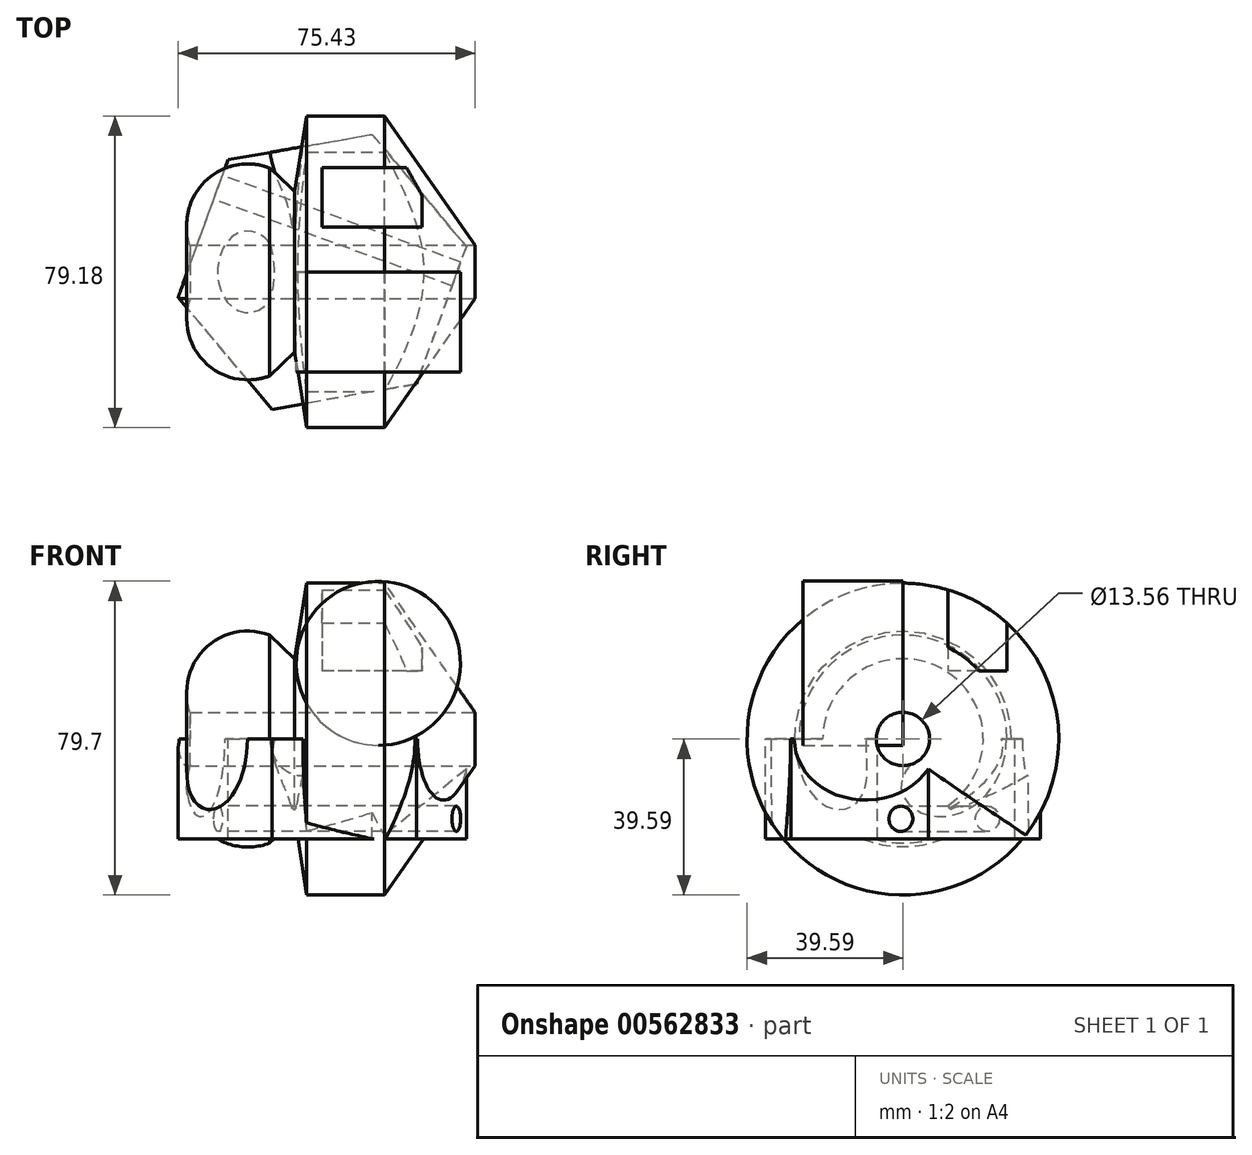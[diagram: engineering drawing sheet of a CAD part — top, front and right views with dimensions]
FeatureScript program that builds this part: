
annotation { "Feature Type Name" : "Feature", "Feature Type Description" : "" }
export const myFeature = defineFeature(function(context is Context, id is Id, definition is map)
    precondition{}
    {
        {
            var Q0;
            Q0=qCreatedBy(makeId("Top.planeOp"),FACE);
            var sketch = newSketch(context, id + "F0", { "sketchPlane" : qUnion([Q0])});
            skCircle(sketch, "E0.cCircle", {"center": v(0, 0) * mm, "radius": 32.2 * mm, "construction": true});
            skLineSegment(sketch, "E0.0", {"start": v(12.7, 34.93) * mm, "end": v(36.6, 6.47) * mm});
            skLineSegment(sketch, "E0.1", {"start": v(36.6, 6.47) * mm, "end": v(23.9, -28.47) * mm});
            skLineSegment(sketch, "E0.2", {"start": v(23.9, -28.47) * mm, "end": v(-12.7, -34.93) * mm});
            skLineSegment(sketch, "E0.3", {"start": v(-12.7, -34.93) * mm, "end": v(-36.6, -6.47) * mm});
            skLineSegment(sketch, "E0.4", {"start": v(-36.6, -6.47) * mm, "end": v(-23.9, 28.47) * mm});
            skLineSegment(sketch, "E0.5", {"start": v(-23.9, 28.47) * mm, "end": v(12.7, 34.93) * mm});
            skPoint(sketch, "E0.0.midPoint", {"position": v(24.65, 20.7) * mm});
            skSolve(sketch);
        }
        {
            var Q0;
            Q0=sQuery(id+"F0.wireOp",EDGE,"E0.5");
            cPlane(context, id + "F1", {"entities" : qUnion([Q0]), "cplaneType" : CPlaneType.LINE_ANGLE, "offset" : 25.4 * mm, "angle" : 30 * degree, "width" : 152.4 * mm, "height" : 152.4 * mm});
        }
        {
            var Q0;
            Q0=makeQuery(id+"F0.imprint","IMPRINT",FACE,{"disambiguationData":[TD([[makeQuery(id+"F0.imprint","IMPRINT",EDGE,{"derivedFrom":sQuery(id+"F0.wireOp",EDGE,"E0.0")}),-1.0]])]});
            extrude(context, id + "F2", {"entities" : qUnion([Q0]), "oppositeDirection" : true, "depth" : 25.4 * mm, "offsetDistance" : 25.4 * mm});
        }
        {
            var Q0;
            Q0=qCreatedBy(id+"F1.planeOp",FACE);
            var sketch = newSketch(context, id + "F3", { "sketchPlane" : qUnion([Q0])});
            skCircle(sketch, "E1", {"center": v(1.06, -15.94) * mm, "radius": 8.14 * mm});
            skSolve(sketch);
        }
        {
            var Q0;
            Q0 = qSketchRegion(id + "F3", true);
            extrude(context, id + "F4", {"entities" : qUnion([Q0]), "operationType" : NewBodyOperationType.REMOVE, "oppositeDirection" : true, "depth" : 25.4 * mm, "offsetDistance" : 25.4 * mm});
        }
        {
            var Q0;
            Q0=qCreatedBy(makeId("Front.planeOp"),FACE);
            var sketch = newSketch(context, id + "F5", { "sketchPlane" : qUnion([Q0])});
            skLineSegment(sketch, "E2", {"start": v(0, 0) * mm, "end": v(0, 49.38) * mm, "construction": true});
            skArc(sketch, "E3", {"start": v(-13.35, 26.42) * mm, "mid": v(-32.29, 19.78) * mm, "end": v(-28.87, 0) * mm});
            skLineSegment(sketch, "E4", {"start": v(-13.35, 26.42) * mm, "end": v(-6.97, 20.4) * mm});
            skLineSegment(sketch, "E5", {"start": v(-6.97, 20.4) * mm, "end": v(-3.96, 39.6) * mm});
            skLineSegment(sketch, "E6", {"start": v(-3.96, 39.6) * mm, "end": v(15.84, 39.6) * mm});
            skLineSegment(sketch, "E7", {"start": v(15.84, 39.6) * mm, "end": v(43.57, 0) * mm});
            skLineSegment(sketch, "E8", {"start": v(43.57, 0) * mm, "end": v(-28.87, 0) * mm});
            skSolve(sketch);
        }
        {
            var Q0;
            Q0=makeQuery(id+"F5.imprint","IMPRINT",FACE,{"disambiguationData":[TD([[makeQuery(id+"F5.imprint","IMPRINT",EDGE,{"derivedFrom":sQuery(id+"F5.wireOp",EDGE,"E3")}),1.0]])]});
            var Q1;
            Q1=sQuery(id+"F5.wireOp",EDGE,"E8");
            revolve(context, id + "F6", {"operationType" : NewBodyOperationType.ADD, "entities" : qUnion([Q0]), "axis" : qUnion([Q1]), "revolveType" : RevolveType.FULL});
        }
        {
            var Q0;
            Q0=qCreatedBy(makeId("Right.planeOp"),FACE);
            var sketch = newSketch(context, id + "F7", { "sketchPlane" : qUnion([Q0])});
            skCircle(sketch, "E9", {"center": v(0, 0) * mm, "radius": 6.78 * mm});
            skSolve(sketch);
        }
        {
            var Q0;
            Q0 = qSketchRegion(id + "F7", true);
            extrude(context, id + "F8", {"entities" : qUnion([Q0]), "operationType" : NewBodyOperationType.REMOVE, "endBound" : BoundingType.SYMMETRIC, "oppositeDirection" : true, "depth" : 152.4 * mm, "offsetDistance" : 25.4 * mm});
        }
        {
            var Q0;
            Q0=makeQuery(id+"F2.opExtrude","SWEPT_FACE",FACE,{"disambiguationData":[OSD([sQuery(id+"F0.wireOp",EDGE,"E0.4")])]});
            var sketch = newSketch(context, id + "F9", { "sketchPlane" : qUnion([Q0])});
            skCircle(sketch, "E10", {"center": v(-11.15, -20.26) * mm, "radius": 3.22 * mm});
            skSolve(sketch);
        }
        {
            var Q0;
            Q0 = qSketchRegion(id + "F9", true);
            extrude(context, id + "F10", {"entities" : qUnion([Q0]), "operationType" : NewBodyOperationType.REMOVE, "oppositeDirection" : true, "depth" : 68.33 * mm, "offsetDistance" : 25.4 * mm});
        }
        {
            var Q0;
            Q0=qCreatedBy(makeId("Right.planeOp"),FACE);
            var sketch = newSketch(context, id + "F11", { "sketchPlane" : qUnion([Q0])});
            skLineSegment(sketch, "E11.bottom", {"start": v(26.47, 40.14) * mm, "end": v(11.38, 40.14) * mm});
            skLineSegment(sketch, "E11.top", {"start": v(26.47, 17.36) * mm, "end": v(11.38, 17.36) * mm});
            skLineSegment(sketch, "E11.left", {"start": v(26.47, 40.14) * mm, "end": v(26.47, 17.36) * mm});
            skLineSegment(sketch, "E11.right", {"start": v(11.38, 40.14) * mm, "end": v(11.38, 17.36) * mm});
            skSolve(sketch);
        }
        {
            var Q0;
            Q0 = qSketchRegion(id + "F11", true);
            extrude(context, id + "F12", {"entities" : qUnion([Q0]), "operationType" : NewBodyOperationType.REMOVE, "depth" : 25.4 * mm, "offsetDistance" : 25.4 * mm});
        }
        {
            var Q0;
            Q0=qCreatedBy(makeId("Front.planeOp"),FACE);
            var sketch = newSketch(context, id + "F13", { "sketchPlane" : qUnion([Q0])});
            skCircle(sketch, "E12", {"center": v(14.26, 19.25) * mm, "radius": 20.86 * mm});
            skSolve(sketch);
        }
        {
            var Q0;
            Q0 = qSketchRegion(id + "F13", true);
            extrude(context, id + "F14", {"entities" : qUnion([Q0]), "depth" : 25.4 * mm, "offsetDistance" : 25.4 * mm});
        }
    });
